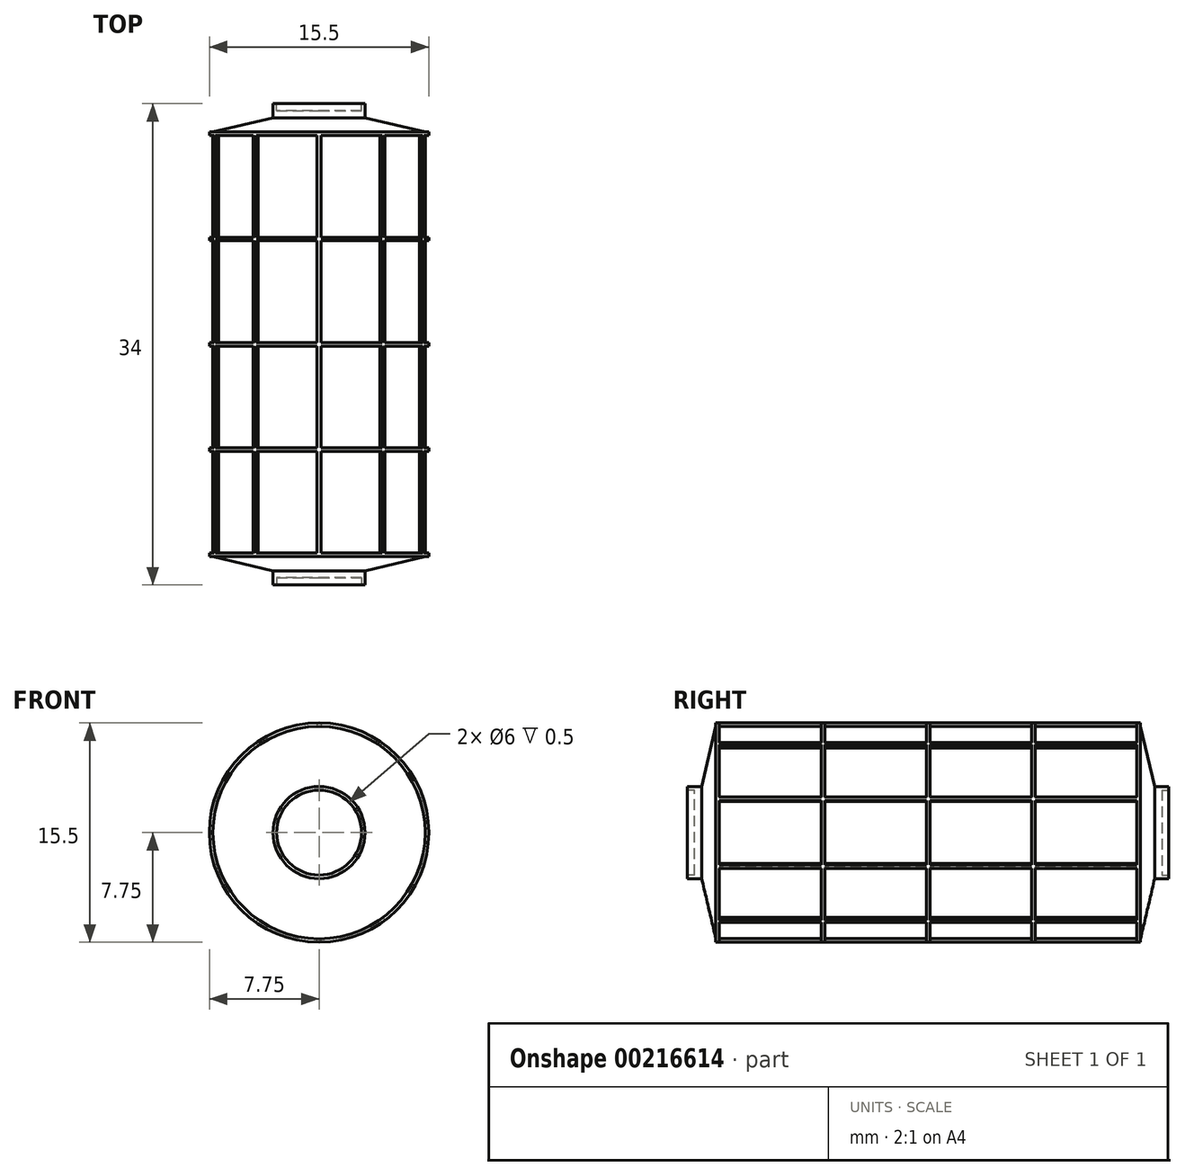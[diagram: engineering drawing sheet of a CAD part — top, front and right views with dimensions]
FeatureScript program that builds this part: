
annotation { "Feature Type Name" : "Feature", "Feature Type Description" : "" }
export const myFeature = defineFeature(function(context is Context, id is Id, definition is map)
    precondition{}
    {
        {
            var Q0;
            Q0=qCreatedBy(makeId("Front.planeOp"),FACE);
            var sketch = newSketch(context, id + "F0", { "sketchPlane" : qUnion([Q0])});
            skCircle(sketch, "E0", {"center": v(0, 0) * mm, "radius": 3.25 * mm});
            skSolve(sketch);
        }
        {
            var Q0;
            Q0=makeQuery(id+"F0.imprint","IMPRINT",FACE,{"disambiguationData":[TD([[makeQuery(id+"F0.imprint","IMPRINT",EDGE,{"derivedFrom":sQuery(id+"F0.wireOp",EDGE,"E0")}),1.0]])]});
            extrude(context, id + "F1", {"entities" : qUnion([Q0]), "depth" : 1 * mm});
        }
        {
            var Q0;
            Q0=makeQuery(id+"F1.opExtrude","CAP_FACE",FACE,{"disambiguationData":[OSD([sQuery(id+"F0.wireOp",EDGE,"E0")])],"isStart":false});
            var sketch = newSketch(context, id + "F2", { "sketchPlane" : qUnion([Q0])});
            skCircle(sketch, "E1", {"center": v(0, 0) * mm, "radius": 3 * mm});
            skSolve(sketch);
        }
        {
            var Q0;
            Q0=makeQuery(id+"F2.imprint","IMPRINT",FACE,{"disambiguationData":[TD([[makeQuery(id+"F2.imprint","IMPRINT",EDGE,{"derivedFrom":sQuery(id+"F2.wireOp",EDGE,"E1")}),1.0]])]});
            extrude(context, id + "F3", {"entities" : qUnion([Q0]), "operationType" : NewBodyOperationType.REMOVE, "oppositeDirection" : true, "depth" : .5 * mm});
        }
        {
            var Q0;
            Q0=qCreatedBy(makeId("Front.planeOp"),FACE);
            cPlane(context, id + "F4", {"entities" : qUnion([Q0]), "cplaneType" : CPlaneType.OFFSET, "offset" : 1 * mm, "oppositeDirection" : true, "width" : 150 * mm, "height" : 150 * mm});
        }
        {
            var Q0;
            Q0=qCreatedBy(id+"F4.planeOp",FACE);
            var sketch = newSketch(context, id + "F5", { "sketchPlane" : qUnion([Q0])});
            skCircle(sketch, "E2", {"center": v(0, 0) * mm, "radius": 7.5 * mm});
            skSolve(sketch);
        }
        {
            var Q1;
            Q1=makeQuery(id+"F1.opExtrude","CAP_FACE",FACE,{"disambiguationData":[OSD([sQuery(id+"F0.wireOp",EDGE,"E0")])],"isStart":true});
            var Q2;
            Q2=makeQuery(id+"F5.imprint","IMPRINT",FACE,{"disambiguationData":[TD([[makeQuery(id+"F5.imprint","IMPRINT",EDGE,{"derivedFrom":sQuery(id+"F5.wireOp",EDGE,"E2")}),1.0]])]});
            loft(context, id + "F6", {"operationType" : NewBodyOperationType.ADD, "sheetProfilesArray" : [{ "sheetProfileEntities" : qUnion([Q1]) }, { "sheetProfileEntities" : qUnion([Q2]) }]});
        }
        {
            var Q0;
            Q0=makeQuery(id+"F6.opLoft","CAP_FACE",FACE,{"disambiguationData":[OSD([makeQuery(id+"F5.imprint","IMPRINT",FACE,{"disambiguationData":[TD([[makeQuery(id+"F5.imprint","IMPRINT",EDGE,{"derivedFrom":sQuery(id+"F5.wireOp",EDGE,"E2")}),1.0]])]})])],"isStart":true});
            extrude(context, id + "F7", {"entities" : qUnion([Q0]), "operationType" : NewBodyOperationType.ADD, "depth" : 30 * mm});
        }
        {
            var Q0;
            Q0=qCreatedBy(makeId("Front.planeOp"),FACE);
            cPlane(context, id + "F8", {"entities" : qUnion([Q0]), "cplaneType" : CPlaneType.OFFSET, "offset" : 32 * mm, "oppositeDirection" : true, "width" : 150 * mm, "height" : 150 * mm});
        }
        {
            var Q0;
            Q0=qCreatedBy(id+"F8.planeOp",FACE);
            var sketch = newSketch(context, id + "F9", { "sketchPlane" : qUnion([Q0])});
            skCircle(sketch, "E3", {"center": v(0, 0) * mm, "radius": 3.25 * mm});
            skSolve(sketch);
        }
        {
            var Q1;
            Q1=makeQuery(id+"F7.opExtrude","CAP_FACE",FACE,{"disambiguationData":[OSD([makeQuery(id+"F5.imprint","IMPRINT",FACE,{"disambiguationData":[TD([[makeQuery(id+"F5.imprint","IMPRINT",EDGE,{"derivedFrom":sQuery(id+"F5.wireOp",EDGE,"E2")}),1.0]])]})])],"isStart":false});
            var Q2;
            Q2=makeQuery(id+"F9.imprint","IMPRINT",FACE,{"disambiguationData":[TD([[makeQuery(id+"F9.imprint","IMPRINT",EDGE,{"derivedFrom":sQuery(id+"F9.wireOp",EDGE,"E3")}),1.0]])]});
            loft(context, id + "F10", {"operationType" : NewBodyOperationType.ADD, "sheetProfilesArray" : [{ "sheetProfileEntities" : qUnion([Q1]) }, { "sheetProfileEntities" : qUnion([Q2]) }]});
        }
        {
            var Q0;
            Q0=makeQuery(id+"F10.opLoft","CAP_FACE",FACE,{"disambiguationData":[OSD([makeQuery(id+"F9.imprint","IMPRINT",FACE,{"disambiguationData":[TD([[makeQuery(id+"F9.imprint","IMPRINT",EDGE,{"derivedFrom":sQuery(id+"F9.wireOp",EDGE,"E3")}),1.0]])]})])],"isStart":true});
            extrude(context, id + "F11", {"entities" : qUnion([Q0]), "operationType" : NewBodyOperationType.ADD, "depth" : 1 * mm});
        }
        {
            var Q0;
            Q0=makeQuery(id+"F11.opExtrude","CAP_FACE",FACE,{"disambiguationData":[OSD([makeQuery(id+"F9.imprint","IMPRINT",FACE,{"disambiguationData":[TD([[makeQuery(id+"F9.imprint","IMPRINT",EDGE,{"derivedFrom":sQuery(id+"F9.wireOp",EDGE,"E3")}),1.0]])]})])],"isStart":false});
            var sketch = newSketch(context, id + "F12", { "sketchPlane" : qUnion([Q0])});
            skCircle(sketch, "E4", {"center": v(0, 0) * mm, "radius": 3 * mm});
            skSolve(sketch);
        }
        {
            var Q0;
            Q0=makeQuery(id+"F12.imprint","IMPRINT",FACE,{"disambiguationData":[TD([[makeQuery(id+"F12.imprint","IMPRINT",EDGE,{"derivedFrom":sQuery(id+"F12.wireOp",EDGE,"E4")}),1.0]])]});
            extrude(context, id + "F13", {"entities" : qUnion([Q0]), "operationType" : NewBodyOperationType.REMOVE, "oppositeDirection" : true, "depth" : .5 * mm});
        }
        {
            var Q0;
            Q0=qCreatedBy(id+"F4.planeOp",FACE);
            var sketch = newSketch(context, id + "F14", { "sketchPlane" : qUnion([Q0])});
            skArc(sketch, "E5", {"start": v(0.13, 7.5) * mm, "mid": v(0, 7.5) * mm, "end": v(-0.13, 7.5) * mm});
            skArc(sketch, "E6", {"start": v(0.14, 7.75) * mm, "mid": v(0, 7.75) * mm, "end": v(-0.14, 7.75) * mm});
            skLineSegment(sketch, "E7", {"start": v(-0.13, 7.5) * mm, "end": v(-0.14, 7.75) * mm});
            skLineSegment(sketch, "E8", {"start": v(0.13, 7.5) * mm, "end": v(0.14, 7.75) * mm});
            skLineSegment(sketch, "E9.1.0", {"start": v(-4.3, 6.14) * mm, "end": v(-4.45, 6.35) * mm});
            skLineSegment(sketch, "E9.1.1", {"start": v(-4.51, 5.99) * mm, "end": v(-4.66, 6.19) * mm});
            skArc(sketch, "E9.1.2", {"start": v(-4.45, 6.35) * mm, "mid": v(-4.56, 6.27) * mm, "end": v(-4.66, 6.19) * mm});
            skArc(sketch, "E9.1.3", {"start": v(-4.3, 6.14) * mm, "mid": v(-4.4, 6.07) * mm, "end": v(-4.51, 5.99) * mm});
            skLineSegment(sketch, "E9.2.0", {"start": v(-7.1, 2.44) * mm, "end": v(-7.33, 2.52) * mm});
            skLineSegment(sketch, "E9.2.1", {"start": v(-7.17, 2.2) * mm, "end": v(-7.41, 2.27) * mm});
            skArc(sketch, "E9.2.2", {"start": v(-7.33, 2.52) * mm, "mid": v(-7.37, 2.4) * mm, "end": v(-7.41, 2.27) * mm});
            skArc(sketch, "E9.2.3", {"start": v(-7.1, 2.44) * mm, "mid": v(-7.13, 2.32) * mm, "end": v(-7.17, 2.2) * mm});
            skLineSegment(sketch, "E9.3.0", {"start": v(-7.17, -2.2) * mm, "end": v(-7.41, -2.27) * mm});
            skLineSegment(sketch, "E9.3.1", {"start": v(-7.1, -2.44) * mm, "end": v(-7.33, -2.52) * mm});
            skArc(sketch, "E9.3.2", {"start": v(-7.41, -2.27) * mm, "mid": v(-7.37, -2.4) * mm, "end": v(-7.33, -2.52) * mm});
            skArc(sketch, "E9.3.3", {"start": v(-7.17, -2.2) * mm, "mid": v(-7.13, -2.32) * mm, "end": v(-7.1, -2.44) * mm});
            skLineSegment(sketch, "E9.4.0", {"start": v(-4.51, -5.99) * mm, "end": v(-4.66, -6.19) * mm});
            skLineSegment(sketch, "E9.4.1", {"start": v(-4.3, -6.14) * mm, "end": v(-4.45, -6.35) * mm});
            skArc(sketch, "E9.4.2", {"start": v(-4.66, -6.19) * mm, "mid": v(-4.56, -6.27) * mm, "end": v(-4.45, -6.35) * mm});
            skArc(sketch, "E9.4.3", {"start": v(-4.51, -5.99) * mm, "mid": v(-4.4, -6.07) * mm, "end": v(-4.3, -6.14) * mm});
            skLineSegment(sketch, "E9.5.0", {"start": v(-0.13, -7.5) * mm, "end": v(-0.14, -7.75) * mm});
            skLineSegment(sketch, "E9.5.1", {"start": v(0.13, -7.5) * mm, "end": v(0.14, -7.75) * mm});
            skArc(sketch, "E9.5.2", {"start": v(-0.14, -7.75) * mm, "mid": v(0, -7.75) * mm, "end": v(0.14, -7.75) * mm});
            skArc(sketch, "E9.5.3", {"start": v(-0.13, -7.5) * mm, "mid": v(0, -7.5) * mm, "end": v(0.13, -7.5) * mm});
            skLineSegment(sketch, "E9.6.0", {"start": v(4.3, -6.14) * mm, "end": v(4.45, -6.35) * mm});
            skLineSegment(sketch, "E9.6.1", {"start": v(4.51, -5.99) * mm, "end": v(4.66, -6.19) * mm});
            skArc(sketch, "E9.6.2", {"start": v(4.45, -6.35) * mm, "mid": v(4.56, -6.27) * mm, "end": v(4.66, -6.19) * mm});
            skArc(sketch, "E9.6.3", {"start": v(4.3, -6.14) * mm, "mid": v(4.4, -6.07) * mm, "end": v(4.51, -5.99) * mm});
            skLineSegment(sketch, "E9.7.0", {"start": v(7.1, -2.44) * mm, "end": v(7.33, -2.52) * mm});
            skLineSegment(sketch, "E9.7.1", {"start": v(7.17, -2.2) * mm, "end": v(7.41, -2.27) * mm});
            skArc(sketch, "E9.7.2", {"start": v(7.33, -2.52) * mm, "mid": v(7.37, -2.4) * mm, "end": v(7.41, -2.27) * mm});
            skArc(sketch, "E9.7.3", {"start": v(7.1, -2.44) * mm, "mid": v(7.13, -2.32) * mm, "end": v(7.17, -2.2) * mm});
            skLineSegment(sketch, "E9.8.0", {"start": v(7.17, 2.2) * mm, "end": v(7.41, 2.27) * mm});
            skLineSegment(sketch, "E9.8.1", {"start": v(7.1, 2.44) * mm, "end": v(7.33, 2.52) * mm});
            skArc(sketch, "E9.8.2", {"start": v(7.41, 2.27) * mm, "mid": v(7.37, 2.4) * mm, "end": v(7.33, 2.52) * mm});
            skArc(sketch, "E9.8.3", {"start": v(7.17, 2.2) * mm, "mid": v(7.13, 2.32) * mm, "end": v(7.1, 2.44) * mm});
            skLineSegment(sketch, "E9.9.0", {"start": v(4.51, 5.99) * mm, "end": v(4.66, 6.19) * mm});
            skLineSegment(sketch, "E9.9.1", {"start": v(4.3, 6.14) * mm, "end": v(4.45, 6.35) * mm});
            skArc(sketch, "E9.9.2", {"start": v(4.66, 6.19) * mm, "mid": v(4.56, 6.27) * mm, "end": v(4.45, 6.35) * mm});
            skArc(sketch, "E9.9.3", {"start": v(4.51, 5.99) * mm, "mid": v(4.4, 6.07) * mm, "end": v(4.3, 6.14) * mm});
            skSolve(sketch);
        }
        {
            var Q0;
            Q0 = qSketchRegion(id + "F14", true);
            extrude(context, id + "F15", {"entities" : qUnion([Q0]), "operationType" : NewBodyOperationType.ADD, "oppositeDirection" : true, "depth" : 30 * mm});
        }
        {
            var Q0;
            Q0=qCreatedBy(makeId("Right.planeOp"),FACE);
            var sketch = newSketch(context, id + "F16", { "sketchPlane" : qUnion([Q0])});
            skLineSegment(sketch, "E10.bottom", {"start": v(1, 7.5) * mm, "end": v(1.25, 7.5) * mm});
            skLineSegment(sketch, "E10.top", {"start": v(1, 7.75) * mm, "end": v(1.25, 7.75) * mm});
            skLineSegment(sketch, "E10.left", {"start": v(1, 7.5) * mm, "end": v(1, 7.75) * mm});
            skLineSegment(sketch, "E10.right", {"start": v(1.25, 7.5) * mm, "end": v(1.25, 7.75) * mm});
            skLineSegment(sketch, "E11.1.0.0", {"start": v(8.44, 7.5) * mm, "end": v(8.69, 7.5) * mm});
            skLineSegment(sketch, "E11.1.0.1", {"start": v(8.44, 7.5) * mm, "end": v(8.44, 7.75) * mm});
            skLineSegment(sketch, "E11.1.0.2", {"start": v(8.69, 7.5) * mm, "end": v(8.69, 7.75) * mm});
            skLineSegment(sketch, "E11.1.0.3", {"start": v(8.44, 7.75) * mm, "end": v(8.69, 7.75) * mm});
            skLineSegment(sketch, "E11.2.0.0", {"start": v(15.87, 7.5) * mm, "end": v(16.12, 7.5) * mm});
            skLineSegment(sketch, "E11.2.0.1", {"start": v(15.87, 7.5) * mm, "end": v(15.87, 7.75) * mm});
            skLineSegment(sketch, "E11.2.0.2", {"start": v(16.12, 7.5) * mm, "end": v(16.12, 7.75) * mm});
            skLineSegment(sketch, "E11.2.0.3", {"start": v(15.87, 7.75) * mm, "end": v(16.12, 7.75) * mm});
            skLineSegment(sketch, "E11.3.0.0", {"start": v(23.31, 7.5) * mm, "end": v(23.56, 7.5) * mm});
            skLineSegment(sketch, "E11.3.0.1", {"start": v(23.31, 7.5) * mm, "end": v(23.31, 7.75) * mm});
            skLineSegment(sketch, "E11.3.0.2", {"start": v(23.56, 7.5) * mm, "end": v(23.56, 7.75) * mm});
            skLineSegment(sketch, "E11.3.0.3", {"start": v(23.31, 7.75) * mm, "end": v(23.56, 7.75) * mm});
            skLineSegment(sketch, "E11.4.0.0", {"start": v(30.75, 7.5) * mm, "end": v(31, 7.5) * mm});
            skLineSegment(sketch, "E11.4.0.1", {"start": v(30.75, 7.5) * mm, "end": v(30.75, 7.75) * mm});
            skLineSegment(sketch, "E11.4.0.2", {"start": v(31, 7.5) * mm, "end": v(31, 7.75) * mm});
            skLineSegment(sketch, "E11.4.0.3", {"start": v(30.75, 7.75) * mm, "end": v(31, 7.75) * mm});
            skLineSegment(sketch, "E11.direction1", {"start": v(1, 7.5) * mm, "end": v(8.44, 7.5) * mm, "construction": true});
            skSolve(sketch);
        }
        {
            var Q0;
            Q0 = qSketchRegion(id + "F16", true);
            var Q1;
            Q1=makeQuery(id+"F6.opLoft","SWEPT_FACE",FACE,{"disambiguationData":[OSD([sQuery(id+"F0.wireOp",EDGE,"E0"),sQuery(id+"F5.wireOp",EDGE,"E2")])]});
            revolve(context, id + "F17", {"operationType" : NewBodyOperationType.ADD, "entities" : qUnion([Q0]), "axis" : qUnion([Q1]), "revolveType" : RevolveType.FULL});
        }
    });
